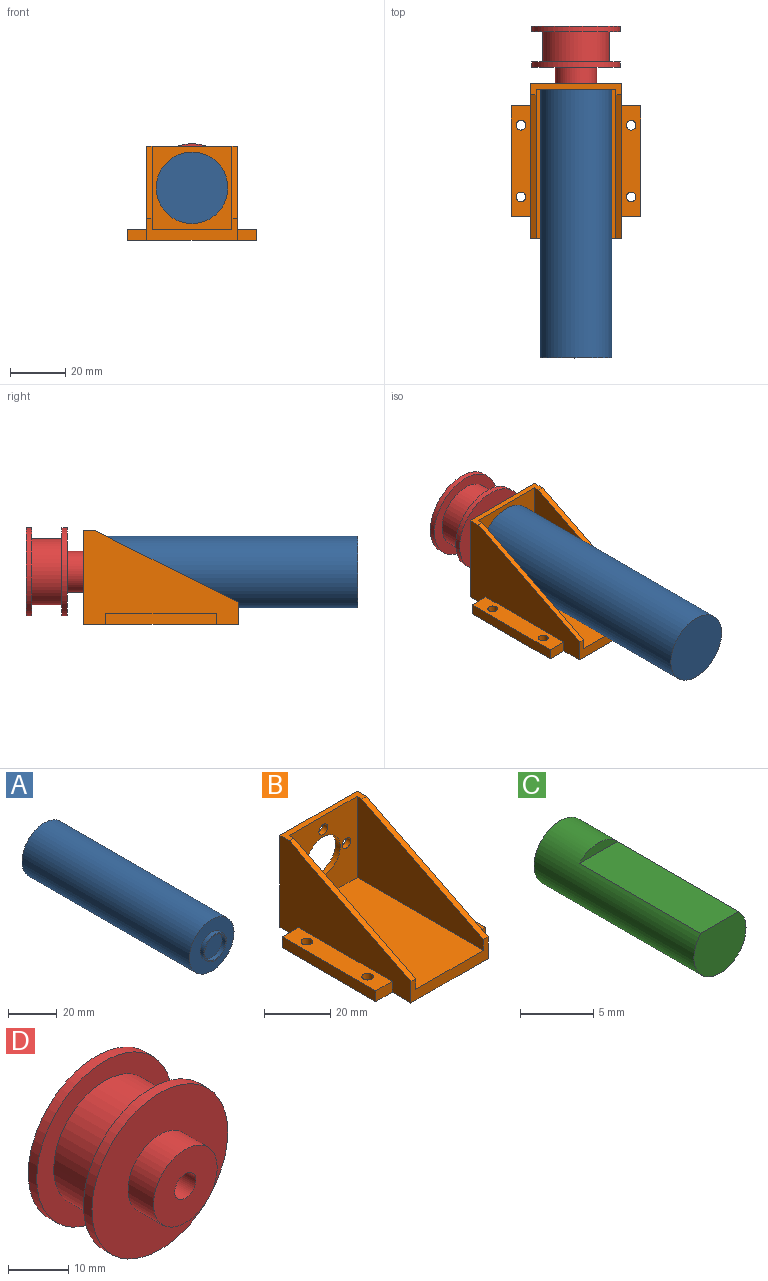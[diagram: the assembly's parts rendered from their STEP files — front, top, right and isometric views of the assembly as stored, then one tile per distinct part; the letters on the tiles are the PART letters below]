
ASSEMBLY  parts=4 mates=3
PART A: 7 faces, bbox 26x99.4x26 mm
  f0: cylinder r=13mm len=97.44mm, axis (0,1,0), area 7959mm2, adj f1,f2
  f1: plane 26x26mm, normal (0,-1,0), area 393.7mm2, adj f0,f4
  f2: plane 26x26mm, normal (0,1,0), area 530.9mm2, adj f0
  f3: cylinder r=6.07mm len=12.15mm, axis (0,1,0), area 76.3mm2, adj f5,f6
  f4: cylinder r=6.61mm len=13.22mm, axis (0,1,0), area 83.1mm2, adj f1,f5
  f5: plane 13.22x13.22mm, normal (0,-1,0), area 21.3mm2, adj f3,f4
  f6: plane 12.15x12.15mm, normal (0,-1,0), area 115.9mm2, adj f3
PART B: 29 faces, bbox 47x56x34 mm
  f0: plane 56x34mm, normal (1,0,0), area 1068mm2, adj f1,f2,f3,f5,f10,f15,f17,f22
  f1: plane 33x8mm, normal (0,-1,0), area 148mm2, adj f0,f9,f17,f18,f19,f21,f22,f23
  f2: plane 33x4mm, normal (0,0,1), area 74mm2, adj f0,f5,f9,f19,f20,f21,f22,f23
  f3: plane 40x7mm, normal (0,0,1), area 260.8mm2, adj f0,f10,f11,f12,f13,f15
  f4: plane 40x7mm, normal (0,0,1), area 260.8mm2, adj f6,f7,f8,f9,f14,f16
  f5: plane 34x33mm, normal (0,1,0), area 913.9mm2, adj f0,f2,f9,f17,f24,f25,f26,f27
  f6: plane 7x4mm, normal (0,1,0), area 28mm2, adj f4,f7,f9,f17
  f7: plane 40x4mm, normal (-1,0,0), area 160mm2, adj f4,f6,f8,f17
  f8: plane 7x4mm, normal (0,-1,0), area 28mm2, adj f4,f7,f9,f17
  f9: plane 56x34mm, normal (-1,0,0), area 1068mm2, adj f1,f2,f4,f5,f6,f8,f17,f23
  f10: plane 7x4mm, normal (0,-1,0), area 28mm2, adj f0,f3,f11,f17
  f11: plane 40x4mm, normal (1,0,0), area 160mm2, adj f3,f10,f15,f17
  f12: cylinder r=1.75mm len=4mm, axis (0,0,1), area 44mm2, adj f3,f17
  f13: cylinder r=1.75mm len=4mm, axis (0,0,1), area 44mm2, adj f3,f17
  f14: cylinder r=1.75mm len=4mm, axis (0,0,1), area 44mm2, adj f4,f17
  f15: plane 7x4mm, normal (0,1,0), area 28mm2, adj f0,f3,f11,f17
  f16: cylinder r=1.75mm len=4mm, axis (0,0,1), area 44mm2, adj f4,f17
  f17: plane 56x47mm, normal (0,0,-1), area 2369.5mm2, adj f0,f1,f5,f6,f7,f8,f9,f10
  f18: plane 54x29mm, normal (0,0,1), area 1566mm2, adj f1,f19,f20,f21
  f19: plane 54x30mm, normal (1,0,0), area 944mm2, adj f1,f2,f18,f20,f23
  f20: plane 30x29mm, normal (0,-1,0), area 661.9mm2, adj f2,f18,f19,f21,f24,f25,f26,f27
  f21: plane 54x30mm, normal (-1,0,0), area 944mm2, adj f1,f2,f18,f20,f22
  f22: plane 52x26mm, normal (0,-0.45,0.89), area 116.3mm2, adj f0,f1,f2,f21
  f23: plane 52x26mm, normal (0,-0.45,0.89), area 116.3mm2, adj f1,f2,f9,f19
  f24: cylinder r=1.85mm len=3.7mm, axis (0,-1,0), area 23.2mm2, adj f5,f20
  f25: cylinder r=1.85mm len=3.7mm, axis (0,-1,0), area 23.2mm2, adj f5,f20
  f26: cylinder r=1.85mm len=3.7mm, axis (0,-1,0), area 23.2mm2, adj f5,f20
  f27: cylinder r=7.25mm len=14.5mm, axis (0,-1,0), area 91.1mm2, adj f5,f20
  f28: cylinder r=1.85mm len=3.7mm, axis (0,-1,0), area 23.2mm2, adj f5,f20
PART C: 5 faces, bbox 5x15.5x5 mm
  f0: cylinder r=2.52mm len=15.46mm, axis (0,1,0), area 196.4mm2, adj f1,f2,f3,f4
  f1: plane 5.04x4.24mm, normal (0,-1,0), area 17.9mm2, adj f0,f3
  f2: plane 5.04x5.04mm, normal (0,1,0), area 20mm2, adj f0
  f3: plane 11.75x3.67mm, normal (0,0,1), area 43.2mm2, adj f0,f1,f4
  f4: plane 3.67x0.8mm, normal (0,-1,0), area 2mm2, adj f0,f3
PART D: 10 faces, bbox 32x21x32 mm
  f0: cylinder r=12mm len=24mm, axis (0,1,0), area 829.4mm2, adj f2,f7
  f1: cylinder r=16mm len=32mm, axis (0,1,0), area 201.1mm2, adj f2,f3
  f2: plane 32x32mm, normal (0,-1,0), area 351.9mm2, adj f0,f1
  f3: plane 32x32mm, normal (0,1,0), area 784.6mm2, adj f1,f4
  f4: cylinder r=2.5mm len=21mm, axis (0,1,0), area 329.9mm2, adj f3,f9
  f5: plane 32x32mm, normal (0,-1,0), area 627.5mm2, adj f6,f8
  f6: cylinder r=16mm len=32mm, axis (0,-1,0), area 201.1mm2, adj f5,f7
  f7: plane 32x32mm, normal (0,1,0), area 351.9mm2, adj f0,f6
  f8: cylinder r=7.5mm len=15mm, axis (0,1,0), area 282.7mm2, adj f5,f9
  f9: plane 15x15mm, normal (0,-1,0), area 157.1mm2, adj f4,f8
PLACE A rot(axis=(0.71,0,-0.71),180deg) t=(-3.25,-62.3,9.11)mm
PLACE B t=(-3.25,9.14,-5.89)mm fixed
PLACE C rot(axis=(1,0,0),180deg) t=(-3.25,-62.3,9.11)mm
PLACE D rot(axis=(0,1,0),0deg) t=(-3.25,58.1,9.11)mm
MATE revolute C.f0 <-> D.f0  axis (0,1,0) through (-3.25,50.6,9.11)mm
MATE revolute C.f0 <-> A.f3  axis (0,-1,0) through (-3.25,35.14,9.11)mm
MATE fastened B.f27 <-> A.f0  axis (0,-1,0) through (-3.25,35.14,9.11)mm
